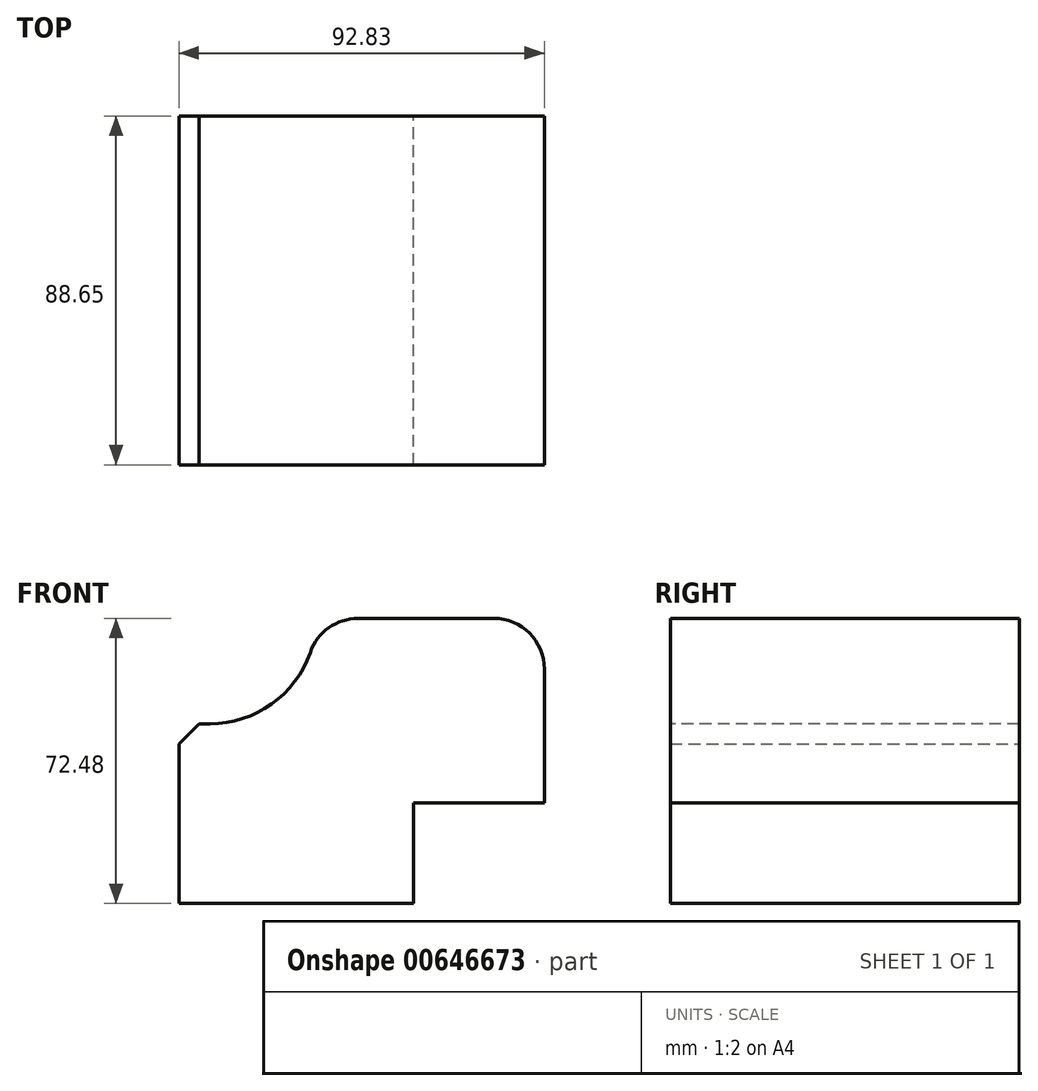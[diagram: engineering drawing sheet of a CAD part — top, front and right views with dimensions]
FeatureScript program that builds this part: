
annotation { "Feature Type Name" : "Feature", "Feature Type Description" : "" }
export const myFeature = defineFeature(function(context is Context, id is Id, definition is map)
    precondition{}
    {
        {
            var Q0;
            Q0=qCreatedBy(makeId("Front.planeOp"),FACE);
            var sketch = newSketch(context, id + "F0", { "sketchPlane" : qUnion([Q0])});
            skLineSegment(sketch, "E0.bottom", {"start": v(-68.05, 45.68) * mm, "end": v(-35.38, 45.68) * mm});
            skLineSegment(sketch, "E0.top", {"start": v(-68.05, 0) * mm, "end": v(-8.45, 0) * mm});
            skLineSegment(sketch, "E0.left", {"start": v(-68.05, 45.68) * mm, "end": v(-68.05, 0) * mm});
            skLineSegment(sketch, "E0.right", {"start": v(-8.45, 25.6) * mm, "end": v(-8.45, 0) * mm});
            skLineSegment(sketch, "E1.bottom", {"start": v(-8.45, 25.6) * mm, "end": v(24.78, 25.6) * mm});
            skLineSegment(sketch, "E1.top", {"start": v(-35.38, 72.48) * mm, "end": v(24.78, 72.48) * mm});
            skLineSegment(sketch, "E1.left", {"start": v(-35.38, 45.68) * mm, "end": v(-35.38, 72.48) * mm});
            skLineSegment(sketch, "E1.right", {"start": v(24.78, 25.6) * mm, "end": v(24.78, 72.48) * mm});
            skSolve(sketch);
        }
        {
            var Q0;
            Q0 = qSketchRegion(id + "F0", true);
            extrude(context, id + "F1", {"entities" : qUnion([Q0]), "depth" : 88.65 * mm, "offsetDistance" : 25.4 * mm});
        }
        {
            var Q0;
            Q0=makeQuery(id+"F1.opExtrude","SWEPT_EDGE",EDGE,{"disambiguationData":[OSD([sQuery(id+"F0.wireOp",EDGE,"E1.top"),sQuery(id+"F0.wireOp",EDGE,"E1.right")])]});
            var Q1;
            Q1=makeQuery(id+"F1.opExtrude","SWEPT_EDGE",EDGE,{"disambiguationData":[OSD([sQuery(id+"F0.wireOp",EDGE,"E1.top"),sQuery(id+"F0.wireOp",EDGE,"E1.left")])]});
            fillet(context, id + "F2", {"entities" : qUnion([Q0, Q1]), "radius" : 12.88 * mm, "tangentPropagation" : true, "allowEdgeOverflow" : false});
        }
        {
            var Q0;
            Q0=makeQuery(id+"F1.opExtrude","SWEPT_EDGE",EDGE,{"disambiguationData":[OSD([sQuery(id+"F0.wireOp",EDGE,"E0.bottom"),sQuery(id+"F0.wireOp",EDGE,"E1.left")])]});
            fillet(context, id + "F3", {"entities" : qUnion([Q0]), "radius" : 26.98 * mm, "tangentPropagation" : true, "allowEdgeOverflow" : false});
        }
        {
            var Q0;
            Q0=makeQuery(id+"F1.opExtrude","SWEPT_EDGE",EDGE,{"disambiguationData":[OSD([sQuery(id+"F0.wireOp",EDGE,"E0.bottom"),sQuery(id+"F0.wireOp",EDGE,"E0.left")])]});
            chamfer(context, id + "F4", {"entities" : qUnion([Q0]), "width" : 5.08 * mm, "tangentPropagation" : true});
        }
    });
